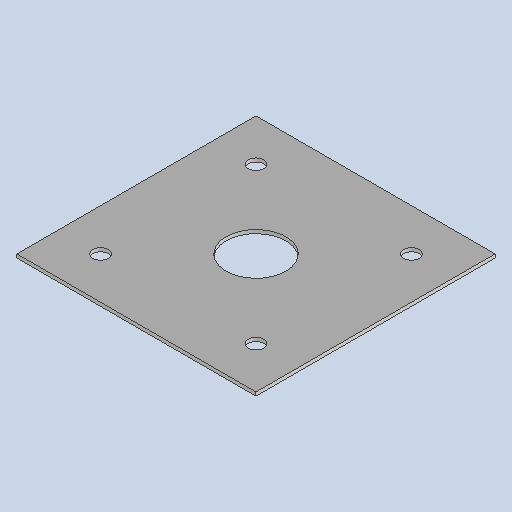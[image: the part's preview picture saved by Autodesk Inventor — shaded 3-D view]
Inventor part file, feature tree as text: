
AUTODESK INVENTOR PART (.ipt)
format: ipt  version: 2025 (Build 290162010, 162A)  size: 289,792 bytes
history: native  units: mm
features: sketch x5, other x5, mirror x2, sheet_metal_op x1, extrude x1, pattern_linear x1
ambient origin geometry x8: Origin, YZ Plane, XZ Plane, XY Plane, X Axis, Y Axis, Z Axis, Center Point
bodies: Solid1 (feature_tree)
feature tree (15):
  sheet_metal_op  "Face1"
  extrude  "Extrusion3"  Depth=200.0mm
  pattern_linear  "Rectangular Pattern2"  Count1=20  [1 undecoded]
  mirror  "Mirror1"
  mirror  "Mirror2"
  sketch  "Sketch1"  dims[d2=3.0mm d25=200.0mm d26=200.0mm]
  other  "Plate1"
  sketch  "Sketch6"  dims[d37=30.0mm]
  sketch  "Sketch8"  dims[d38=150.0mm]
  sketch  "Sketch9"  dims[d39=3.0mm]
  sketch  "Sketch10"  dims[d40=0.0mm d48=13.0mm d49=25.0mm d50=0.0mm d51=0.0mm d52=30.0mm d54=72.0mm d55=13.0mm d57=3.0mm d58=0.0mm d73=65.0mm d74=65.0mm d75=50.0mm d76=3.0mm d77=0.0mm]
  other  "Cut1"
  other  "Cut2"
  other  "Cut3"
  other  "Definition1"
note: 1 required parameter value undecoded (feature->parameter linkage not recoverable at this tier; creation-order binding heuristic only, values carry confidence <= 0.55)
